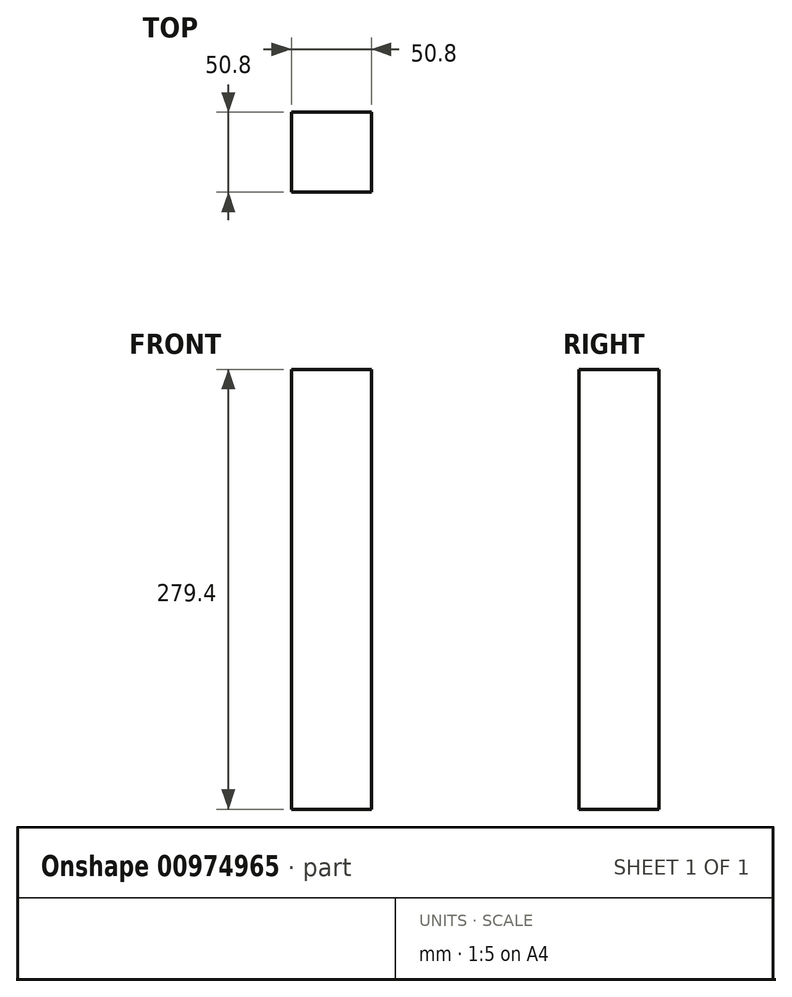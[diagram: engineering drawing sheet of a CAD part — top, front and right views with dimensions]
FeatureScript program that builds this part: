
annotation { "Feature Type Name" : "Feature", "Feature Type Description" : "" }
export const myFeature = defineFeature(function(context is Context, id is Id, definition is map)
    precondition{}
    {
        {
            var Q0;
            Q0=qCreatedBy(makeId("Front.planeOp"),FACE);
            var sketch = newSketch(context, id + "F0", { "sketchPlane" : qUnion([Q0])});
            skLineSegment(sketch, "E0.bottom", {"start": v(-53.1, 118.56) * mm, "end": v(-2.3, 118.56) * mm});
            skLineSegment(sketch, "E0.top", {"start": v(-53.1, -160.84) * mm, "end": v(-2.3, -160.84) * mm});
            skLineSegment(sketch, "E0.left", {"start": v(-53.1, 118.56) * mm, "end": v(-53.1, -160.84) * mm});
            skLineSegment(sketch, "E0.right", {"start": v(-2.3, 118.56) * mm, "end": v(-2.3, -160.84) * mm});
            skSolve(sketch);
        }
        {
            var Q0;
            Q0=makeQuery(id+"F0.imprint","IMPRINT",FACE,{"disambiguationData":[TD([[makeQuery(id+"F0.imprint","IMPRINT",EDGE,{"derivedFrom":sQuery(id+"F0.wireOp",EDGE,"E0.bottom")}),-1.0]])]});
            extrude(context, id + "F1", {"entities" : qUnion([Q0]), "depth" : 50.8 * mm, "offsetDistance" : 25.4 * mm});
        }
    });
